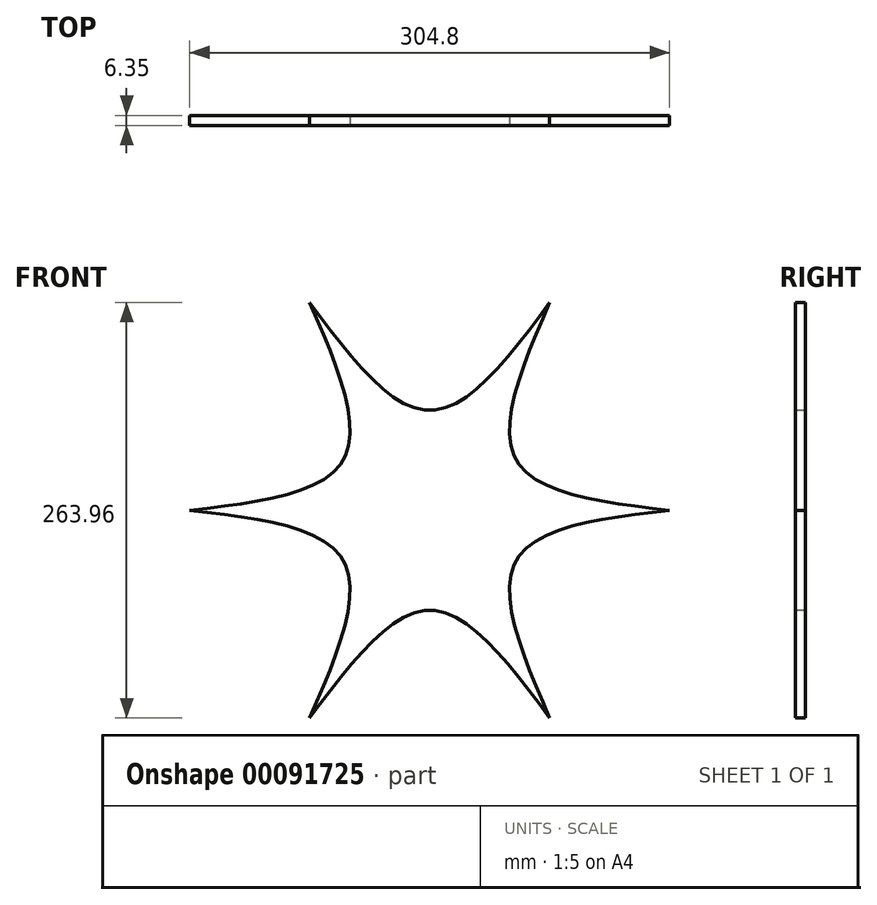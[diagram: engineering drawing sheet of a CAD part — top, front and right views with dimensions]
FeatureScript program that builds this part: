
annotation { "Feature Type Name" : "Feature", "Feature Type Description" : "" }
export const myFeature = defineFeature(function(context is Context, id is Id, definition is map)
    precondition{}
    {
        {
            var Q0;
            Q0=qCreatedBy(makeId("Front.planeOp"),FACE);
            var sketch = newSketch(context, id + "F0", { "sketchPlane" : qUnion([Q0])});
            skLineSegment(sketch, "E0.0", {"start": v(152.4, 0) * mm, "end": v(76.2, -131.98) * mm});
            skLineSegment(sketch, "E0.1", {"start": v(76.2, -131.98) * mm, "end": v(-76.2, -131.98) * mm});
            skLineSegment(sketch, "E0.2", {"start": v(-76.2, -131.98) * mm, "end": v(-152.4, 0) * mm});
            skLineSegment(sketch, "E0.3", {"start": v(-152.4, 0) * mm, "end": v(-76.2, 131.98) * mm});
            skLineSegment(sketch, "E0.4", {"start": v(-76.2, 131.98) * mm, "end": v(76.2, 131.98) * mm});
            skLineSegment(sketch, "E0.5", {"start": v(76.2, 131.98) * mm, "end": v(152.4, 0) * mm});
            skLineSegment(sketch, "E1", {"start": v(-114.3, 66) * mm, "end": v(114.3, -66) * mm, "construction": true});
            skLineSegment(sketch, "E2", {"start": v(114.3, 66) * mm, "end": v(-114.3, -66) * mm, "construction": true});
            skLineSegment(sketch, "E3", {"start": v(0, 131.98) * mm, "end": v(0, -131.98) * mm, "construction": true});
            skCircle(sketch, "E4", {"center": v(0, 0) * mm, "radius": 63.5 * mm, "construction": true});
            skLineSegment(sketch, "E5", {"start": v(-76.2, -131.98) * mm, "end": v(76.2, 131.98) * mm});
            skLineSegment(sketch, "E6", {"start": v(-76.2, 131.98) * mm, "end": v(76.2, -131.98) * mm});
            skLineSegment(sketch, "E7", {"start": v(152.4, 0) * mm, "end": v(-152.4, 0) * mm});
            skFitSpline(sketch, "E8", {"points": [v(-76.2, 131.98) * mm, v(0, 63.5) * mm, v(76.2, 131.98) * mm], "startDerivative": vector(152.4, -205.45) * mm, "endDerivative": vector(152.4, 205.45) * mm});
            skFitSpline(sketch, "E9", {"points": [v(76.2, 131.98) * mm, v(55, 31.75) * mm, v(152.4, 0) * mm], "startDerivative": vector(-101.72, -234.7) * mm, "endDerivative": vector(254.12, -29.26) * mm});
            skFitSpline(sketch, "E10", {"points": [v(152.4, 0) * mm, v(55, -31.75) * mm, v(76.2, -131.98) * mm], "startDerivative": vector(-254.12, -29.26) * mm, "endDerivative": vector(101.72, -234.7) * mm});
            skFitSpline(sketch, "E11", {"points": [v(76.2, -131.98) * mm, v(0, -63.5) * mm, v(-76.2, -131.98) * mm], "startDerivative": vector(-152.4, 205.45) * mm, "endDerivative": vector(-152.4, -205.45) * mm});
            skFitSpline(sketch, "E12", {"points": [v(-76.2, -131.98) * mm, v(-55, -31.75) * mm, v(-152.4, 0) * mm], "startDerivative": vector(101.72, 234.7) * mm, "endDerivative": vector(-254.12, 29.26) * mm});
            skFitSpline(sketch, "E13", {"points": [v(-152.4, 0) * mm, v(-55, 31.75) * mm, v(-76.2, 131.98) * mm], "startDerivative": vector(254.12, 29.26) * mm, "endDerivative": vector(-101.72, 234.7) * mm});
            skSolve(sketch);
        }
        {
            var Q0;
            {var subQ0=sQuery(id+"F0.wireOp",EDGE,"E13");Q0=makeQuery(id+"F0.imprint","IMPRINT",FACE,{"disambiguationData":[TD([[makeQuery(id+"F0.imprint","IMPRINT",EDGE,{"derivedFrom":subQ0}),-1.0]])]});}
            var Q1;
            {var subQ0=sQuery(id+"F0.wireOp",EDGE,"E8");Q1=makeQuery(id+"F0.imprint","IMPRINT",FACE,{"disambiguationData":[TD([[makeQuery(id+"F0.imprint","IMPRINT",EDGE,{"derivedFrom":subQ0}),-1.0]])]});}
            var Q2;
            {var subQ0=sQuery(id+"F0.wireOp",EDGE,"E9");Q2=makeQuery(id+"F0.imprint","IMPRINT",FACE,{"disambiguationData":[TD([[makeQuery(id+"F0.imprint","IMPRINT",EDGE,{"derivedFrom":subQ0}),-1.0]])]});}
            var Q3;
            {var subQ0=sQuery(id+"F0.wireOp",EDGE,"E10");Q3=makeQuery(id+"F0.imprint","IMPRINT",FACE,{"disambiguationData":[TD([[makeQuery(id+"F0.imprint","IMPRINT",EDGE,{"derivedFrom":subQ0}),-1.0]])]});}
            var Q4;
            {var subQ0=sQuery(id+"F0.wireOp",EDGE,"E11");Q4=makeQuery(id+"F0.imprint","IMPRINT",FACE,{"disambiguationData":[TD([[makeQuery(id+"F0.imprint","IMPRINT",EDGE,{"derivedFrom":subQ0}),-1.0]])]});}
            var Q5;
            {var subQ0=sQuery(id+"F0.wireOp",EDGE,"E12");Q5=makeQuery(id+"F0.imprint","IMPRINT",FACE,{"disambiguationData":[TD([[makeQuery(id+"F0.imprint","IMPRINT",EDGE,{"derivedFrom":subQ0}),-1.0]])]});}
            extrude(context, id + "F1", {"entities" : qUnion([Q0, Q1, Q2, Q3, Q4, Q5]), "depth" : 6.35 * mm});
        }
    });
